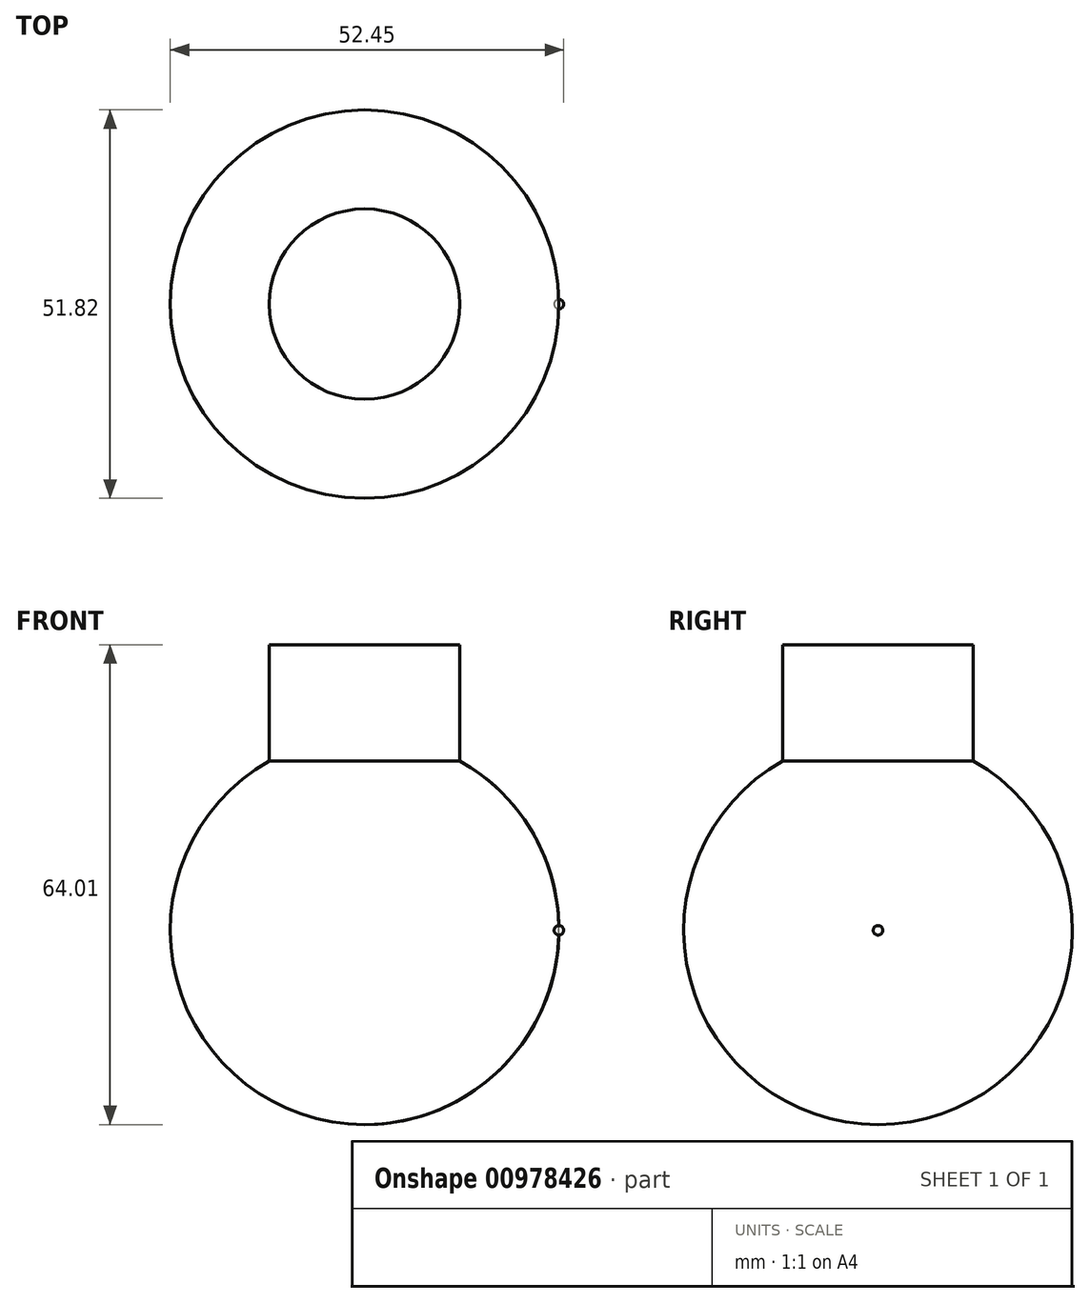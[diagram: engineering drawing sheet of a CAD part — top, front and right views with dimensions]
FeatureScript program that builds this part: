
annotation { "Feature Type Name" : "Feature", "Feature Type Description" : "" }
export const myFeature = defineFeature(function(context is Context, id is Id, definition is map)
    precondition{}
    {
        {
            var Q0;
            Q0=qCreatedBy(makeId("Top.planeOp"),FACE);
            var sketch = newSketch(context, id + "F0", { "sketchPlane" : qUnion([Q0])});
            skCircle(sketch, "E0", {"center": v(0, 0) * mm, "radius": 12.7 * mm});
            skSolve(sketch);
        }
        {
            var Q0;
            Q0=qCreatedBy(makeId("Front.planeOp"),FACE);
            var sketch = newSketch(context, id + "F1", { "sketchPlane" : qUnion([Q0])});
            skLineSegment(sketch, "E1", {"start": v(0, 0) * mm, "end": v(0, -25.9) * mm, "construction": true});
            skLineSegment(sketch, "E2", {"start": v(0, 0) * mm, "end": v(0, 25.9) * mm, "construction": true});
            skArc(sketch, "E3", {"start": v(0, -25.9) * mm, "mid": v(25.9, 0) * mm, "end": v(0, 25.9) * mm});
            skLineSegment(sketch, "E4", {"start": v(0, 25.9) * mm, "end": v(0, -25.9) * mm});
            skSolve(sketch);
        }
        {
            var Q0;
            Q0=makeQuery(id+"F0.imprint","IMPRINT",FACE,{"disambiguationData":[TD([[makeQuery(id+"F0.imprint","IMPRINT",EDGE,{"derivedFrom":sQuery(id+"F0.wireOp",EDGE,"E0")}),1.0]])]});
            extrude(context, id + "F2", {"entities" : qUnion([Q0]), "depth" : 38.1 * mm, "offsetDistance" : 25.4 * mm});
        }
        {
            var Q0;
            Q0 = qSketchRegion(id + "F1", true);
            var Q1;
            Q1=sQuery(id+"F1.wireOp",EDGE,"E4");
            revolve(context, id + "F3", {"operationType" : NewBodyOperationType.ADD, "surfaceOperationType" : NewSurfaceOperationType.NEW, "entities" : qUnion([Q0]), "axis" : qUnion([Q1]), "revolveType" : RevolveType.FULL});
        }
        {
            var Q0;
            Q0=qCreatedBy(makeId("Front.planeOp"),FACE);
            var sketch = newSketch(context, id + "F4", { "sketchPlane" : qUnion([Q0])});
            skLineSegment(sketch, "E5", {"start": v(0, -0.26) * mm, "end": v(25.9, 0) * mm, "construction": true});
            skCircle(sketch, "E6", {"center": v(25.9, 0) * mm, "radius": 0.64 * mm, "construction": true});
            skLineSegment(sketch, "E7", {"start": v(25.9, 0) * mm, "end": v(25.91, -0.63) * mm, "construction": true});
            skLineSegment(sketch, "E8", {"start": v(25.91, -0.63) * mm, "end": v(25.9, 0.63) * mm, "construction": true});
            skArc(sketch, "E9", {"start": v(25.91, -0.63) * mm, "mid": v(26.54, 0) * mm, "end": v(25.9, 0.63) * mm});
            skLineSegment(sketch, "E10", {"start": v(25.9, 0.63) * mm, "end": v(25.91, -0.63) * mm});
            skSolve(sketch);
        }
        {
            var Q0;
            Q0=makeQuery(id+"F4.imprint","IMPRINT",FACE,{"disambiguationData":[TD([[makeQuery(id+"F4.imprint","IMPRINT",EDGE,{"derivedFrom":sQuery(id+"F4.wireOp",EDGE,"E9")}),1.0]])]});
            var Q1;
            Q1=sQuery(id+"F4.wireOp",EDGE,"E10");
            revolve(context, id + "F5", {"surfaceOperationType" : NewSurfaceOperationType.NEW, "entities" : qUnion([Q0]), "axis" : qUnion([Q1]), "revolveType" : RevolveType.FULL});
        }
    });
